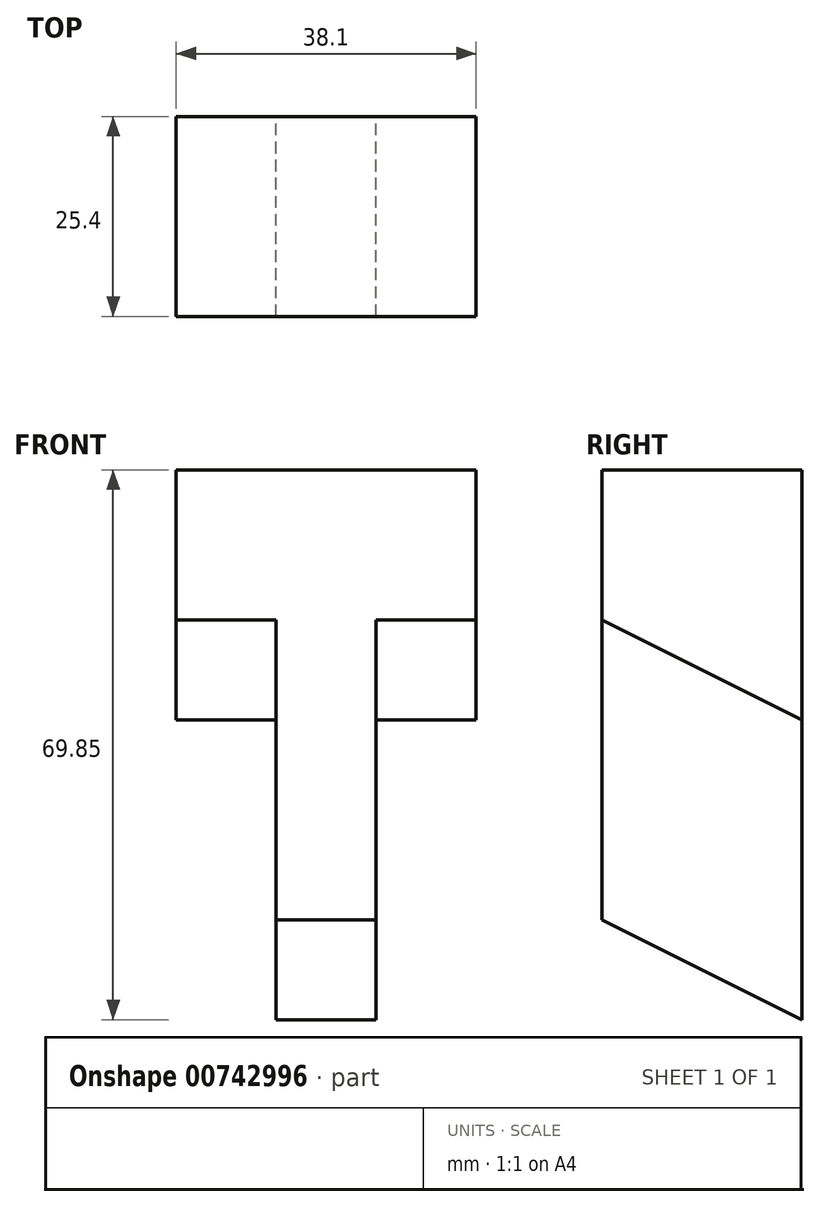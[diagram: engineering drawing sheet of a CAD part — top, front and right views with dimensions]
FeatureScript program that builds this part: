
annotation { "Feature Type Name" : "Feature", "Feature Type Description" : "" }
export const myFeature = defineFeature(function(context is Context, id is Id, definition is map)
    precondition{}
    {
        {
            var Q0;
            Q0=qCreatedBy(makeId("Front.planeOp"),FACE);
            var sketch = newSketch(context, id + "F0", { "sketchPlane" : qUnion([Q0])});
            skLineSegment(sketch, "E0", {"start": v(0, 0) * mm, "end": v(12.7, 0) * mm});
            skLineSegment(sketch, "E1", {"start": v(12.7, 0) * mm, "end": v(12.7, 38.1) * mm});
            skLineSegment(sketch, "E2", {"start": v(12.7, 38.1) * mm, "end": v(25.4, 38.1) * mm});
            skLineSegment(sketch, "E3", {"start": v(25.4, 38.1) * mm, "end": v(25.4, 69.85) * mm});
            skLineSegment(sketch, "E4", {"start": v(-12.7, 69.85) * mm, "end": v(25.4, 69.85) * mm});
            skLineSegment(sketch, "E5", {"start": v(-12.7, 69.85) * mm, "end": v(-12.7, 38.1) * mm});
            skLineSegment(sketch, "E6", {"start": v(-12.7, 38.1) * mm, "end": v(0, 38.1) * mm});
            skLineSegment(sketch, "E7", {"start": v(0, 38.1) * mm, "end": v(0, 0) * mm});
            skSolve(sketch);
        }
        {
            var Q0;
            Q0 = qSketchRegion(id + "F0", true);
            extrude(context, id + "F1", {"entities" : qUnion([Q0]), "depth" : 25.4 * mm, "offsetDistance" : 25.4 * mm});
        }
        {
            var Q0;
            Q0=makeQuery(id+"F1.opExtrude","SWEPT_FACE",FACE,{"disambiguationData":[OSD([sQuery(id+"F0.wireOp",EDGE,"E1")])]});
            var sketch = newSketch(context, id + "F2", { "sketchPlane" : qUnion([Q0])});
            skLineSegment(sketch, "E8", {"start": v(-25.4, 12.7) * mm, "end": v(0, 0) * mm});
            skSolve(sketch);
        }
        {
            var Q0;
            Q0 = qSketchRegion(id + "F2", true);
            var Q1;
            {var subQ0=sQuery(id+"F2.wireOp",EDGE,"E8");Q1=makeQuery(id+"F2.imprint","IMPRINT",FACE,{"disambiguationData":[TD([[makeQuery(id+"F2.imprint","IMPRINT",EDGE,{"derivedFrom":subQ0}),-1.0]])]});}
            extrude(context, id + "F3", {"entities" : qUnion([Q0, Q1]), "operationType" : NewBodyOperationType.REMOVE, "oppositeDirection" : true, "depth" : 25.4 * mm, "offsetDistance" : 25.4 * mm});
        }
        {
            var Q0;
            Q0=makeQuery(id+"F1.opExtrude","SWEPT_FACE",FACE,{"disambiguationData":[OSD([sQuery(id+"F0.wireOp",EDGE,"E3")])]});
            var sketch = newSketch(context, id + "F4", { "sketchPlane" : qUnion([Q0])});
            skLineSegment(sketch, "E9", {"start": v(-25.4, 50.8) * mm, "end": v(0, 38.1) * mm});
            skSolve(sketch);
        }
        {
            var Q0;
            {var subQ0=sQuery(id+"F4.wireOp",EDGE,"E9");Q0=makeQuery(id+"F4.imprint","IMPRINT",FACE,{"disambiguationData":[TD([[makeQuery(id+"F4.imprint","IMPRINT",EDGE,{"derivedFrom":subQ0}),-1.0]])]});}
            extrude(context, id + "F5", {"entities" : qUnion([Q0]), "operationType" : NewBodyOperationType.REMOVE, "oppositeDirection" : true, "depth" : 12.7 * mm, "offsetDistance" : 25.4 * mm});
        }
        {
            var Q0;
            Q0=makeQuery(id+"F1.opExtrude","SWEPT_FACE",FACE,{"disambiguationData":[OSD([sQuery(id+"F0.wireOp",EDGE,"E5")])]});
            var sketch = newSketch(context, id + "F6", { "sketchPlane" : qUnion([Q0])});
            skLineSegment(sketch, "E10", {"start": v(25.4, 50.8) * mm, "end": v(0, 38.1) * mm});
            skSolve(sketch);
        }
        {
            var Q0;
            {var subQ0=sQuery(id+"F6.wireOp",EDGE,"E10");Q0=makeQuery(id+"F6.imprint","IMPRINT",FACE,{"disambiguationData":[TD([[makeQuery(id+"F6.imprint","IMPRINT",EDGE,{"derivedFrom":subQ0}),1.0]])]});}
            extrude(context, id + "F7", {"entities" : qUnion([Q0]), "operationType" : NewBodyOperationType.REMOVE, "oppositeDirection" : true, "depth" : 12.7 * mm, "offsetDistance" : 25.4 * mm});
        }
    });
